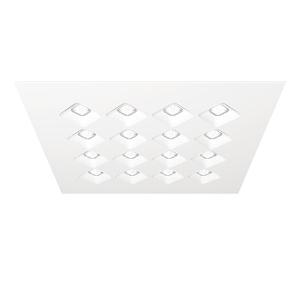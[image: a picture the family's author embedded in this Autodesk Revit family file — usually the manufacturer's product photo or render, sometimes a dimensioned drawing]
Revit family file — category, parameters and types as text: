
# Revit family: 3f_filippi_-_3f_diagon_3f_filippi_-_23415_-_3f_diagon_39w-840_dali_621x621
name_source: partatom
category: Lighting Fixtures
units: mm (PartAtom-declared; Revit-internal decimal feet)

## family parameters
Cut with Voids When Loaded = No
Host = Face
Light Source = No
Part Type = Normal
Room Calculation Point = No
Round Connector Dimension = Use Diameter
Shared = No

## types (1)
- 3F Filippi - 3F Dìagon (1 x LED, 5796 lm, 40 W, 4000 K)
    Apparent Load = 40 VA
    Approval mark = CE
    CIE Flux Codes = 67 96 100 100 100
    Color Rendering = 80
    Color Temperature = 4000 K
    Control Gear = Electronic transformer
    Default Elevation = 1800 mm
    Description = ILLUMINOTECHNICAL
Luminous efficiency 100% (DLOR 100%, ULOR 0%).
Initial luminous flux of the luminaire 5796 lm.
Direct symmetric distribution.
Installation Interdistance Transv.D = 1.39 x hu - Long.D = 1.39 x hu.
Average luminance <3000 cd/m² for radial angles >65°.
Tabular UGR (CIE 117 - 4H-8H; S=0.25H; 70/50/20): RUG 18.4 - 18.4.
Beam angle: 93° - 92°.
Luminous efficacy 145 lm/W.
Lifetime (L90/B10): 30000 h. (tq+25°C)
Lifetime (L85/B10): 50000 h. (tq+25°C)
Lifetime (L80/B20): 80000 h. (tq+25°C)
Lifetime (L70/B20): 100000 h. (tq+25°C)
Sudden decreased luminous flux after 50000 hours: 0% (C0).
Photobiological safety in compliance with IEC/TR 62778: RG0 risk exempt, (IEC 62471).
In compliance with IEC/EN 62722-2-1 - IEC/EN 62717 standards.

SOURCE
Squared LED module 39W/840.
Energy efficiency class (UE 2019/2020 - UE 2019/2015): C.
CIE 13.3 Colour rendering index: CRI >80 (R9 <50%).
IES TM-30 Fidelity Index: Rf = 84 Rg = 95.
CCT nominal colour temperature 4000 K.
Colour initial tolerance (MacAdam): SDCM 3.

MECHANICAL
Housing in hot-galvanised steel, painted in white polyester.
Honeycombed diagonal screen in white anti-glare polycarbonate.
Rhomboidal lenses with differentiated surfaces, etched and prismatic to optimise the orientation of the luminous flux, in transparent methacrylate (PMMA).
Luminaire with limited surface temperature. - D - (EN 60598-2-24)
Dimensions: 621x621 mm, height 30 mm. Weight 3.875 kg.
IP43 protection degree for exposed part, IP20 for recessed part.
Mechanical strength to impacts IK06 (1 joule).
Glow-wire test resistance 650°C.

ELECTRICAL
Halogen Free DALI-2, PUSH-DIM, electronic wiring 230V-50/60Hz, power factor 0.97 at full load, THD <25%, constant output current, class I, 1 driver, 1 DALI addresse.
Power of the luminaire 40 W.
ENEC - CE.
SAFE FLICKER: PstLM=<1 and SVM=<0.4 (IEC TR 61547-1 and IEC TR 63158), to ensure a more comfortable and safe light.
Luminaire compliant with EN 60598-2-22 for power supply from a centralised emergency system CPSS (Central Power Supply System), not incorporated in the luminaire - high risk areas excluded. The default power and flux are 100% in AC and 15% in DC.
Ambient temperature from 0°C to +25°C.
Temperature class T6 max 85°C.
Quick connection.
Relative humidity UR: <85%.

INSTALLATION
Lay-in recessed fitting.
Height only 30 mm.
Installation on false ceilings with recessed dimensions greater than 596x596 standard size.
Installation after mounting the false ceiling, resting on the exposed structure, minimum void of 140 mm from the lower edge of the structure.
Simultaneous installation with the false ceiling, minimum void of 60 mm from the lower edge of the structure.
All accessories dedicated to this product are available on the Catalog and on our website www.3F-Filippi.com.

APPLICATIONS
Environments: staterooms, with VDTs, offices.
Environments with exacting visual tasks, where diffused soft light for optimum visual comfort is required.

LIGHT MANAGEMENT
Recommended minimum setting: 10%.
The device, equipped with DALI-2 driver, can be controlled manually with 3F Easy Dim technology or automatically/manually with 3F Smart Dimming technology and/or centralised DALI systems.
DALI-2 certification guarantees interoperability with other devices with the same certification.
In electrical systems without a regulation system (manual or automatic) and DALI bus, a suitable jumper must be made on the DA-DA terminals of the appliance.

WARNING
Luminaire designed for disposal/recycling at end-of-life.
Replaceable (LED only) light source by a professional. Replaceable control gear by a professional.
    Height = 0 mm  [stored 0 ft]
    Lamp = 1 x LED
    Lamp Light Flux = 5796 lm
    Lamp Power = 40 W
    Lamp count = 1
    Length = 621 mm
    Lifetime = 50000 h
    Luminous efficacy = 145 lm/W
    Manufacturer = 3F Filippi
    ModVariant = No
    Model = 3F Filippi - 23415 - 3F Diagon 39W-840 DALI 621x621
    Mounting Place = Ceiling
    Mounting Type = Recessed
    Number of Poles = 1
    OnlyDefault = Yes
    Power Factor = 1
    Product Name = 3F Filippi - 3F Dìagon
    Product group = recessed luminaire
    ProductGroupID = 4
    Protection Class = Protection class I
    Protection Degree = IP 20
    RLX_Detail_Level = 1
    RLX_Emergency_Light_Flux = 0 lm
    RLX_Emergency_Type = 0
    RLX_Emergency_Type_DB = No
    RlxData = <blob elided: 87185 chars, md5=97476fe9>
    Socket = socket
    Standby Power = 0 W
    System Light Flux = 5796 lm
    System Power = 40 W
    Type Comments = Product without accessories
    Type Image = 3ffilippi_3f_diagon.jpg
    URL = http://relux.com
    VarID = ---
    Voltage = 0 V
    Weight = 0.00 kg
    Width = 621 mm

note: [stored X ft] marks values corroborated as IEEE doubles in the binary element streams (Revit-internal decimal feet)

## geometry (parser evidence)
native form markers: Blend x4, Sweep x12
no freeform markers — native parametric forms only
